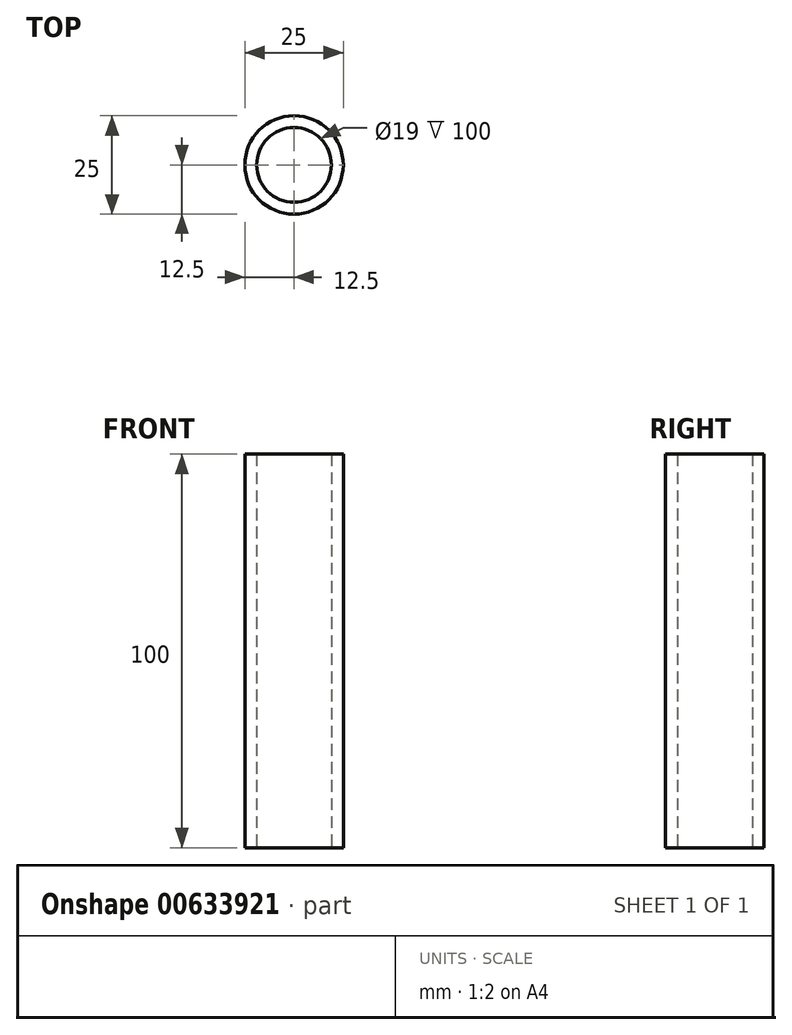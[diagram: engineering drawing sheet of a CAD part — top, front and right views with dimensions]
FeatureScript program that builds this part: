
annotation { "Feature Type Name" : "Feature", "Feature Type Description" : "" }
export const myFeature = defineFeature(function(context is Context, id is Id, definition is map)
    precondition{}
    {
        {
            var Q0;
            Q0=qCreatedBy(makeId("Top.planeOp"),FACE);
            var sketch = newSketch(context, id + "F0", { "sketchPlane" : qUnion([Q0])});
            skCircle(sketch, "E0", {"center": v(0, 0) * mm, "radius": 12.5 * mm});
            skCircle(sketch, "E1", {"center": v(0, 0) * mm, "radius": 9.5 * mm});
            skSolve(sketch);
        }
        {
            var Q0;
            Q0 = qSketchRegion(id + "F0", true);
            extrude(context, id + "F1", {"entities" : qUnion([Q0]), "depth" : 100 * mm, "offsetDistance" : 25 * mm});
        }
        {
            var Q0;
            Q0=makeQuery(id+"F1.opExtrude","CAP_FACE",FACE,{"disambiguationData":[OSD([sQuery(id+"F0.wireOp",EDGE,"E0"),sQuery(id+"F0.wireOp",EDGE,"E1")])],"isStart":false});
            var sketch = newSketch(context, id + "F2", { "sketchPlane" : qUnion([Q0])});
            skCircle(sketch, "E2.0", {"center": v(0, 0) * mm, "radius": 9.5 * mm});
            skCircle(sketch, "E3.0", {"center": v(0, 0) * mm, "radius": 12.5 * mm});
            skSolve(sketch);
        }
    });
